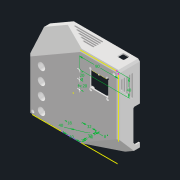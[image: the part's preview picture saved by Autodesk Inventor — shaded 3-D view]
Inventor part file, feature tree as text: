
AUTODESK INVENTOR PART (.ipt)
format: ipt  version: 2022 (Build 260153000, 153)  size: 852,480 bytes
history: native  units: mm
features: extrude x14, sketch x12, projected_geometry x9, fillet x8, other x8, chamfer x6, hole x5, reference x5, shell x1
ambient origin geometry x8: Origin, YZ Plane, XZ Plane, XY Plane, X Axis, Y Axis, Z Axis, Center Point
bodies: Solid1 (feature_tree)
feature tree (68):
  extrude  "Extrusion1"  Depth=2.0mm TaperAngle=45.0deg
  chamfer  "Chamfer1"  Distance=2.0mm Angle=45.0deg
  chamfer  "Chamfer2"  Distance=2.0mm Angle=45.0deg
  chamfer  "Chamfer3"  Distance=3.0mm
  shell  "Shell1"  Thickness=1.0mm
  extrude  "Extrusion2"  Depth=10.0mm
  hole  "Hole2"  [1 undecoded]
  chamfer  "Chamfer4"  Distance=30.0mm
  extrude  "Extrusion3"  Depth=30.0mm
  extrude  "Extrusion4"  Depth=3.0mm
  hole  "Hole3"  [1 undecoded]
  hole  "Hole4"  [1 undecoded]
  sketch  "Sketch12"  dims[d19=8.0mm d20=3.0mm d21=0.0mm]
  extrude  "Extrusion6"  Depth=5.0mm
  extrude  "Extrusion5"  Depth=5.0mm
  extrude  "Extrusion7"  Depth=5.0mm
  chamfer  "Chamfer6"  Distance=7.0mm
  fillet  "Fillet2"  [1 undecoded]
  fillet  "Fillet4"  Radius=3.0mm
  fillet  "Fillet5"  Radius=6.0mm
  fillet  "Fillet7"  Radius=7.0mm
  fillet  "Fillet8"  [1 undecoded]
  extrude  "Extrusion8"  Depth=3.0mm
  extrude  "top intake"  Depth=3.0mm
  extrude  "relay_out"  Depth=3.0mm
  chamfer  "Chamfer7"  Distance=3.0mm
  other  "fan_mount"
  extrude  "fan hole"  Depth=3.0mm
  extrude  "Extrusion14"  Depth=3.0mm TaperAngle=0.0deg
  fillet  "Fillet11"  Radius=2.0mm
  fillet  "Fillet12"  Radius=4.0mm
  hole  "Hole6"  [1 undecoded]
  extrude  "Extrusion15"  Depth=2.0mm
  extrude  "Extrusion12"  Depth=3.0mm
  fillet  "Fillet9"  Radius=20.0mm
  other  "led"
  hole  "Hole7"  [1 undecoded]
  sketch  "Sketch1"  dims[d0=50.0mm d1=0.0mm d2=36.0mm d3=2.0mm d4=45.0deg d5=36.0mm d6=2.0mm d7=45.0deg d8=4.0mm d9=2.0mm d10=45.0deg]
  reference  "Reference1"
  sketch  "Sketch2"  dims[d12=39.0mm]
  sketch  "Sketch4"  dims[d13=42.0mm]
  projected_geometry  "Projected Loop3"
  projected_geometry  "Projected Loop4"
  projected_geometry  "Projected Loop5"
  projected_geometry  "Projected Loop6"
  sketch  "Sketch6"  dims[d14=20.0mm]
  reference  "Reference2"
  sketch  "Sketch7"  dims[d15=20.0mm]
  reference  "Reference3"
  reference  "Reference4"
  sketch  "Sketch8"  dims[d17=8.0mm]
  sketch  "Sketch9"  dims[d18=8.0mm]
  projected_geometry  "Projected Loop9"
  projected_geometry  "Projected Loop10"
  projected_geometry  "Projected Loop11"
  sketch  "Sketch13"  dims[d29=3.6mm d30=6.0mm d31=6.5mm d32=3.4mm d33=90.0deg d34=8.0mm d35=20.594885mm]
  projected_geometry  "Projected Loop12"
  other  "air_intake"
  sketch  "Sketch17"  dims[d36=2.0mm d37=2.0mm d38=45.0deg d39=1.0mm]
  projected_geometry  "Projected Loop13"
  sketch  "Sketch18"  dims[d40=0.0mm d41=0.0mm d42=10.0mm]
  reference  "Reference5"
  sketch  "Sketch20"  dims[d43=10.0mm d44=40.0mm d45=0.0mm d48=3.6mm d49=6.0mm d50=6.8mm d51=30.0mm d52=90.0deg d53=8.0mm d54=20.594885mm d56=30.0mm d57=30.0mm d58=20.0mm d59=30.0mm d60=17.0mm d61=6.0mm d62=26.0mm d63=17.5mm d64=90.0deg d65=8.0mm d66=20.594885mm d71=5.0mm d72=5.0mm d73=5.0mm d74=5.0mm d75=7.0mm d76=0.0mm d82=3.0mm d84=6.0mm d89=7.0mm d90=0.0mm d92=3.0mm d93=3.0mm d94=3.0mm d95=3.0mm d96=22.0mm d97=15.0mm d98=0.0mm d99=8.0mm d100=2.0mm d101=45.0deg d102=4.0mm d104=2.0mm d105=2.0mm d107=1.0mm d108=20.0mm d109=10.0mm d110=20.0mm d111=20.0mm d112=10.0mm d113=10.0mm d115=0.0mm d116=0.0mm d117=2.0mm d118=32.0mm d119=32.0mm d120=3.0mm d121=3.0mm d122=5.0mm d123=3.0mm d124=10.0mm d125=5.0mm d126=5.0mm d127=3.0mm d128=50.0mm d129=0.0mm d130=15.0mm d131=10.0mm d132=10.0mm d133=78.0mm d134=10.0mm d135=0.0mm d136=2.0mm d137=2.0mm d138=45.0deg d139=8.0mm d141=40.0mm d142=40.0mm d143=10.0mm d144=0.0mm d152=2.0mm d153=10.0mm d154=0.0mm d155=40.0mm d156=2.0mm d157=15.4mm d162=4.0mm d163=0.0mm d164=3.0mm d165=3.0mm d166=3.4mm d167=6.0mm d168=6.5mm d169=3.4mm d170=14.3117mm d171=8.0mm d172=20.594885mm d187=4.0mm d188=0.0mm d190=20.0mm d191=3.0mm d192=3.0mm d193=3.0mm d194=3.0mm d195=3.0mm d196=3.0mm d197=3.0mm d198=3.0mm d199=3.0mm d201=20.0mm d202=20.0mm d203=52.0mm d208=5.3mm d209=6.0mm d210=6.5mm d211=3.4mm d212=14.3117mm d213=8.0mm d214=20.594885mm d216=20.0mm d217=20.0mm d218=40.0mm d260=90.0mm d261=18.0mm d262=3.0mm d263=5.0mm d264=3.0mm d265=5.0mm d80=3.0mm d81=0.0mm d83=0.0mm]
  parser-record x1  (decoder bookkeeping rows leaked as tree rows — omitted from the tree; the rows remain in map.json)
  other  "Ensamble.iam"
  other  "base:1"
  other  "Nokia LCD:1"
  other  "Ardi_UNO:1"
note: 7 required parameter values undecoded (feature->parameter linkage not recoverable at this tier; creation-order binding heuristic only, values carry confidence <= 0.55)
note: 1 file-system path scrubbed to <path> (originals preserved in map.json)
